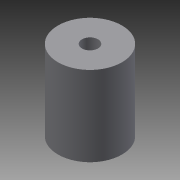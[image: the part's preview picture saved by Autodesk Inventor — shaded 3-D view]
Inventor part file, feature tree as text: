
AUTODESK INVENTOR PART (.ipt)
format: ipt  version: 2013 (Build 170138000, 138)  size: 70,144 bytes
history: native  units: mm
features: extrude x1, sketch x1
ambient origin geometry x8: Origin, YZ Plane, XZ Plane, XY Plane, X Axis, Y Axis, Z Axis, Center Point
bodies: Solid1 (feature_tree)
feature tree (2):
  extrude  "Extrusion1"  Depth=20.0mm
  sketch  "Sketch1"  dims[d0=5.0mm d2=20.0mm d3=25.0mm d4=0.0mm]
